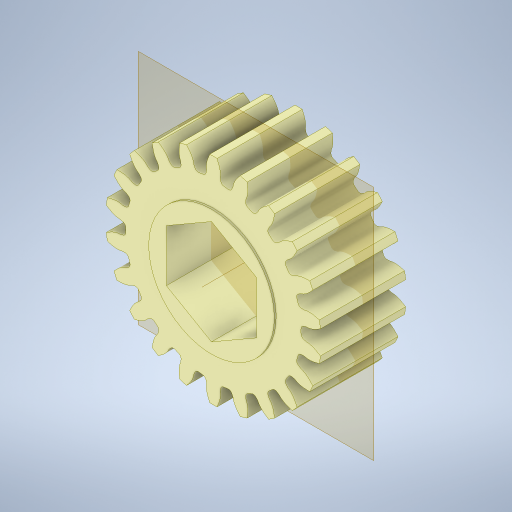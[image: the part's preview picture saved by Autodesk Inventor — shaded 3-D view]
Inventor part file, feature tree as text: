
AUTODESK INVENTOR PART (.ipt)
format: ipt  version: 2023.3 (Build 273359000, 359)  size: 515,072 bytes
history: native  units: in
note: dims shown in document units (in); Inventor stores cm internally (conversion verified against a paired STEP export)
features: other x2, plane x1
ambient origin geometry x8: Origin, YZ Plane, XZ Plane, XY Plane, X Axis, Y Axis, Z Axis, Center Point
bodies: Solid1 (feature_tree)
feature tree (3):
  plane  "Work Plane1"
  other  "Work Axis1"
  other  "Cut-Extrude1"
